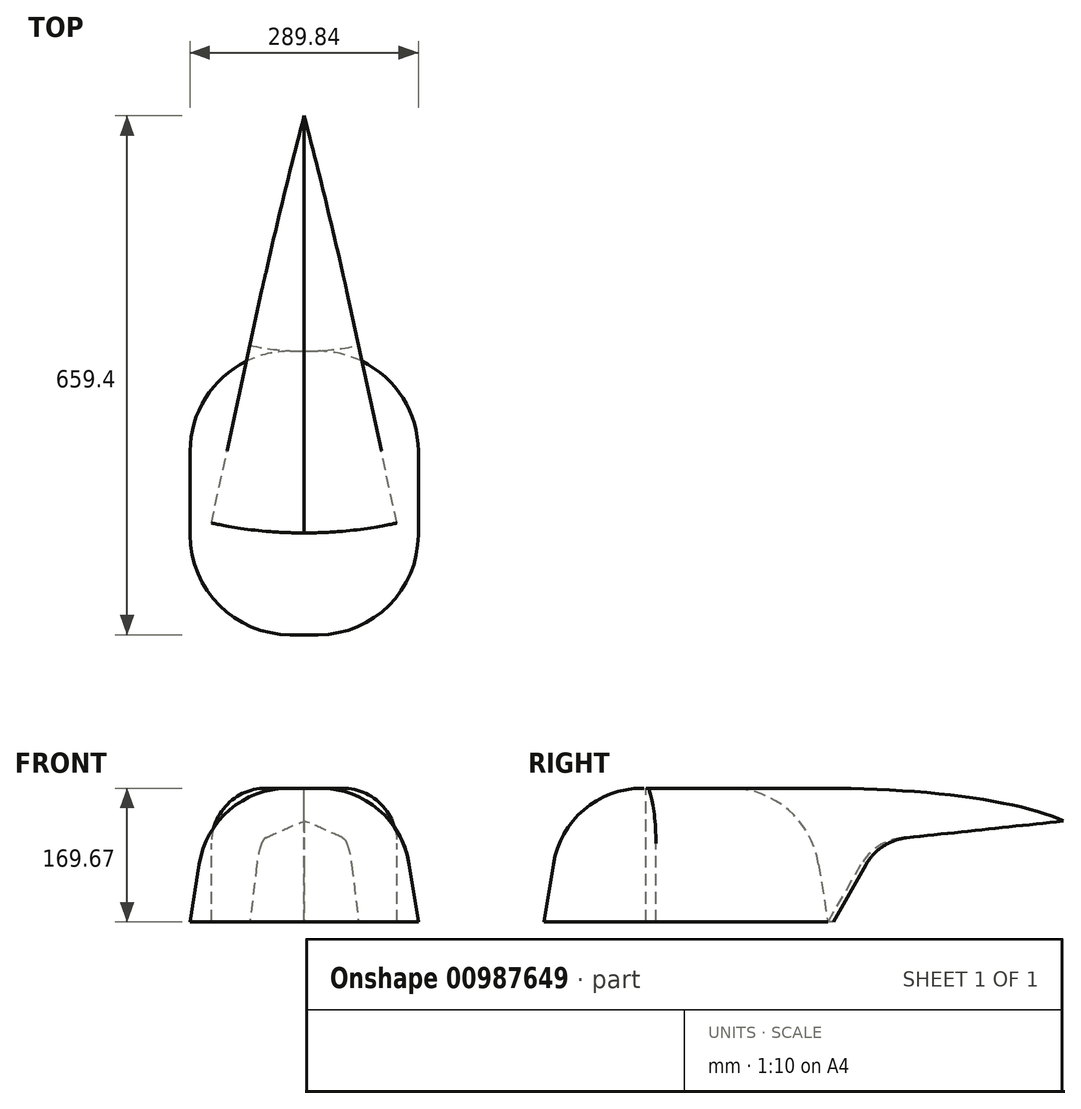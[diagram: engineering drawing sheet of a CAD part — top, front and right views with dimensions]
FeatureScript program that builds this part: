
annotation { "Feature Type Name" : "Feature", "Feature Type Description" : "" }
export const myFeature = defineFeature(function(context is Context, id is Id, definition is map)
    precondition{}
    {
        {
            var Q0;
            Q0=qCreatedBy(makeId("Top.planeOp"),FACE);
            cPlane(context, id + "F0", {"entities" : qUnion([Q0]), "cplaneType" : CPlaneType.OFFSET, "offset" : 56.9 * mm, "width" : 152.4 * mm, "height" : 152.4 * mm});
        }
        {
            var Q0;
            Q0=qCreatedBy(id+"F0.planeOp",FACE);
            var sketch = newSketch(context, id + "F1", { "sketchPlane" : qUnion([Q0])});
            skLineSegment(sketch, "E0.bottom", {"start": v(-132.13, 35.27) * mm, "end": v(132.13, 35.27) * mm});
            skLineSegment(sketch, "E0.left", {"start": v(-132.13, 35.27) * mm, "end": v(-132.13, -35.27) * mm});
            skLineSegment(sketch, "E0.right", {"start": v(132.13, 35.27) * mm, "end": v(132.13, -35.27) * mm});
            skPoint(sketch, "E0.middle", {"position": v(0, 0) * mm});
            skLineSegment(sketch, "E1", {"start": v(-144.92, 0) * mm, "end": v(161.92, 0) * mm, "construction": true});
            skLineSegment(sketch, "E2", {"start": v(0, 227.4) * mm, "end": v(0, -180.1) * mm, "construction": true});
            skLineSegment(sketch, "E3", {"start": v(-17.92, -180.1) * mm, "end": v(0, -180.1) * mm});
            skLineSegment(sketch, "E4", {"start": v(-144.92, -53.1) * mm, "end": v(-144.92, 0) * mm});
            skLineSegment(sketch, "E5.MirrorCS", {"start": v(17.92, -180.1) * mm, "end": v(0, -180.1) * mm});
            skLineSegment(sketch, "E6.MirrorCS", {"start": v(144.92, -53.1) * mm, "end": v(144.92, 0) * mm});
            skPoint(sketch, "E7.visualSharp", {"position": v(-144.92, -180.1) * mm});
            skArc(sketch, "E7.filletArc", {"start": v(-144.92, -53.1) * mm, "mid": v(-107.72, -142.9) * mm, "end": v(-17.92, -180.1) * mm});
            skPoint(sketch, "E8.visualSharp", {"position": v(144.92, -180.1) * mm});
            skArc(sketch, "E8.filletArc", {"start": v(17.92, -180.1) * mm, "mid": v(107.72, -142.9) * mm, "end": v(144.92, -53.1) * mm});
            skLineSegment(sketch, "E9.MirrorCS", {"start": v(-144.92, 53.1) * mm, "end": v(-144.92, 0) * mm});
            skArc(sketch, "E10.MirrorCS", {"start": v(-144.92, 53.1) * mm, "mid": v(-107.72, 142.9) * mm, "end": v(-17.92, 180.1) * mm});
            skLineSegment(sketch, "E11.MirrorCS", {"start": v(-17.92, 180.1) * mm, "end": v(0, 180.1) * mm});
            skLineSegment(sketch, "E12.MirrorCS", {"start": v(17.92, 180.1) * mm, "end": v(0, 180.1) * mm});
            skArc(sketch, "E13.MirrorCS", {"start": v(17.92, 180.1) * mm, "mid": v(107.72, 142.9) * mm, "end": v(144.92, 53.1) * mm});
            skLineSegment(sketch, "E14.MirrorCS", {"start": v(144.92, 53.1) * mm, "end": v(144.92, 0) * mm});
            skSolve(sketch);
        }
        {
            var Q0;
            Q0=makeQuery(id+"F1.imprint","IMPRINT",FACE,{"disambiguationData":[TD([[makeQuery(id+"F1.imprint","IMPRINT",EDGE,{"derivedFrom":sQuery(id+"F1.wireOp",EDGE,"E3")}),1.0]])]});
            extrude(context, id + "F2", {"entities" : qUnion([Q0]), "depth" : 169.67 * mm, "offsetDistance" : 25.4 * mm, "hasDraft" : true, "draftAngle" : 9 * degree, "draftPullDirection" : true});
        }
        {
            var Q0;
            Q0=makeQuery(id+"F2.opExtrude","CAP_EDGE",EDGE,{"disambiguationData":[OSD([sQuery(id+"F1.wireOp",EDGE,"E4"),sQuery(id+"F1.wireOp",EDGE,"E9.MirrorCS")])],"isStart":false});
            fillet(context, id + "F3", {"entities" : qUnion([Q0]), "radius" : 114.3 * mm, "tangentPropagation" : true, "allowEdgeOverflow" : false});
        }
        {
            var Q0;
            Q0=qCreatedBy(makeId("Right.planeOp"),FACE);
            var sketch = newSketch(context, id + "F4", { "sketchPlane" : qUnion([Q0])});
            skLineSegment(sketch, "E15", {"start": v(-50.78, 141.78) * mm, "end": v(-50.78, 226.57) * mm});
            skLineSegment(sketch, "E16", {"start": v(-50.78, 226.57) * mm, "end": v(501.85, 226.57) * mm});
            skLineSegment(sketch, "E17", {"start": v(501.85, 226.57) * mm, "end": v(505.9, 187.63) * mm});
            skLineSegment(sketch, "E18", {"start": v(505.9, 187.63) * mm, "end": v(239.69, 160) * mm});
            skLineSegment(sketch, "E19", {"start": v(239.69, 160) * mm, "end": v(180.07, 56.9) * mm});
            skLineSegment(sketch, "E20", {"start": v(180.07, 56.9) * mm, "end": v(-50.78, 56.9) * mm});
            skLineSegment(sketch, "E21", {"start": v(-50.78, 56.9) * mm, "end": v(-50.78, 141.78) * mm});
            skSolve(sketch);
        }
        {
            var Q0;
            Q0=qCreatedBy(makeId("Right.planeOp"),FACE);
            var sketch = newSketch(context, id + "F5", { "sketchPlane" : qUnion([Q0])});
            skLineSegment(sketch, "E22", {"start": v(507.37, 313.04) * mm, "end": v(507.37, 110.46) * mm, "construction": true});
            skSolve(sketch);
        }
        {
            var Q0;
            Q0=makeQuery(id+"F4.imprint","IMPRINT",FACE,{"disambiguationData":[TD([[makeQuery(id+"F4.imprint","IMPRINT",EDGE,{"derivedFrom":sQuery(id+"F4.wireOp",EDGE,"E15")}),-1.0]])]});
            var Q1;
            Q1=sQuery(id+"F5.wireOp",EDGE,"E22");
            revolve(context, id + "F6", {"surfaceOperationType" : NewSurfaceOperationType.NEW, "entities" : qUnion([Q0]), "axis" : qUnion([Q1]), "revolveType" : RevolveType.ONE_DIRECTION, "angle" : 12.18 * degree});
        }
        {
            var Q0;
            Q0=makeQuery(id+"F6.opRevolve","CAP_EDGE",EDGE,{"disambiguationData":[OSD([sQuery(id+"F4.wireOp",EDGE,"E16")])],"isStart":false});
            var Q1;
            Q1=makeQuery(id+"F6.opRevolve","SWEPT_EDGE",EDGE,{"disambiguationData":[OSD([sQuery(id+"F4.wireOp",EDGE,"E18"),sQuery(id+"F4.wireOp",EDGE,"E19")])]});
            fillet(context, id + "F7", {"entities" : qUnion([Q0, Q1]), "radius" : 69.85 * mm, "tangentPropagation" : true, "allowEdgeOverflow" : false});
        }
        {
            var Q0;
            Q0=makeQuery(id+"F6.opRevolve","SWEPT_BODY",BODY,{"disambiguationData":[OSD([sQuery(id+"F4.wireOp",EDGE,"E15"),sQuery(id+"F4.wireOp",EDGE,"E16"),sQuery(id+"F4.wireOp",EDGE,"E17"),sQuery(id+"F4.wireOp",EDGE,"E18"),sQuery(id+"F4.wireOp",EDGE,"E19"),sQuery(id+"F4.wireOp",EDGE,"E20"),sQuery(id+"F4.wireOp",EDGE,"E21")])]});
            var Q1;
            Q1=qCreatedBy(makeId("Right.planeOp"),FACE);
            mirror(context, id + "F8", {"entities" : qUnion([Q0]), "mirrorPlane" : qUnion([Q1])});
        }
    });
